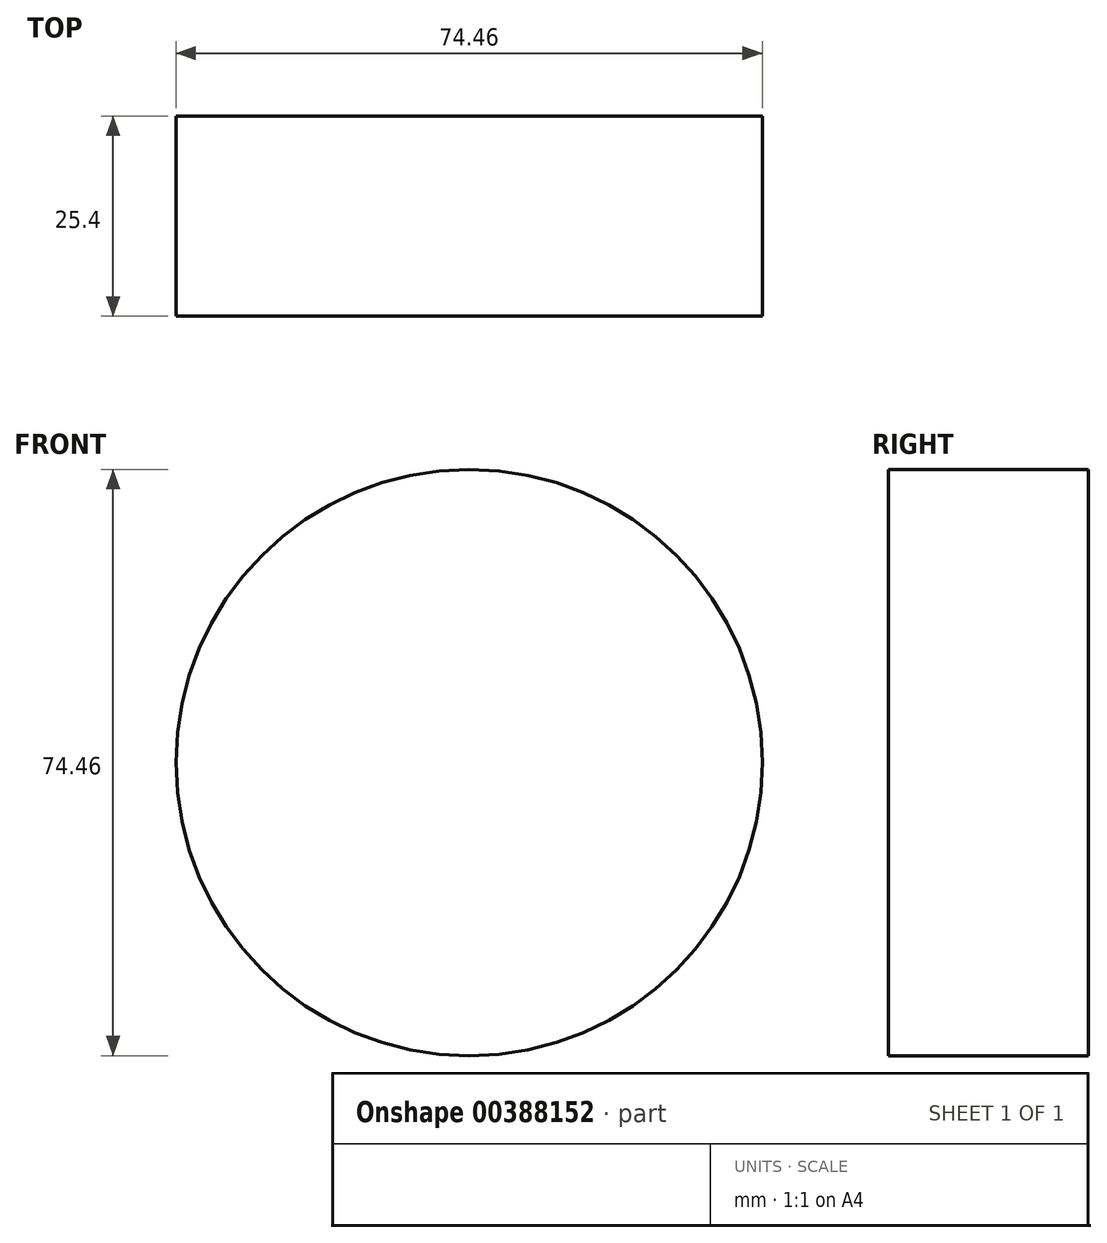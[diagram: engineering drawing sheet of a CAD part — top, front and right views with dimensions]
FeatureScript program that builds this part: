
annotation { "Feature Type Name" : "Feature", "Feature Type Description" : "" }
export const myFeature = defineFeature(function(context is Context, id is Id, definition is map)
    precondition{}
    {
        {
            var Q0;
            Q0=qCreatedBy(makeId("Front.planeOp"),FACE);
            var sketch = newSketch(context, id + "F0", { "sketchPlane" : qUnion([Q0])});
            skCircle(sketch, "E0", {"center": v(0, 0) * mm, "radius": 37.23 * mm});
            skSolve(sketch);
        }
        {
            var Q0;
            Q0=qSketchRegion(id+"F0",true);
            extrude(context, id + "F1", {"entities" : qUnion([Q0]), "depth" : 25.4 * mm});
        }
    });
